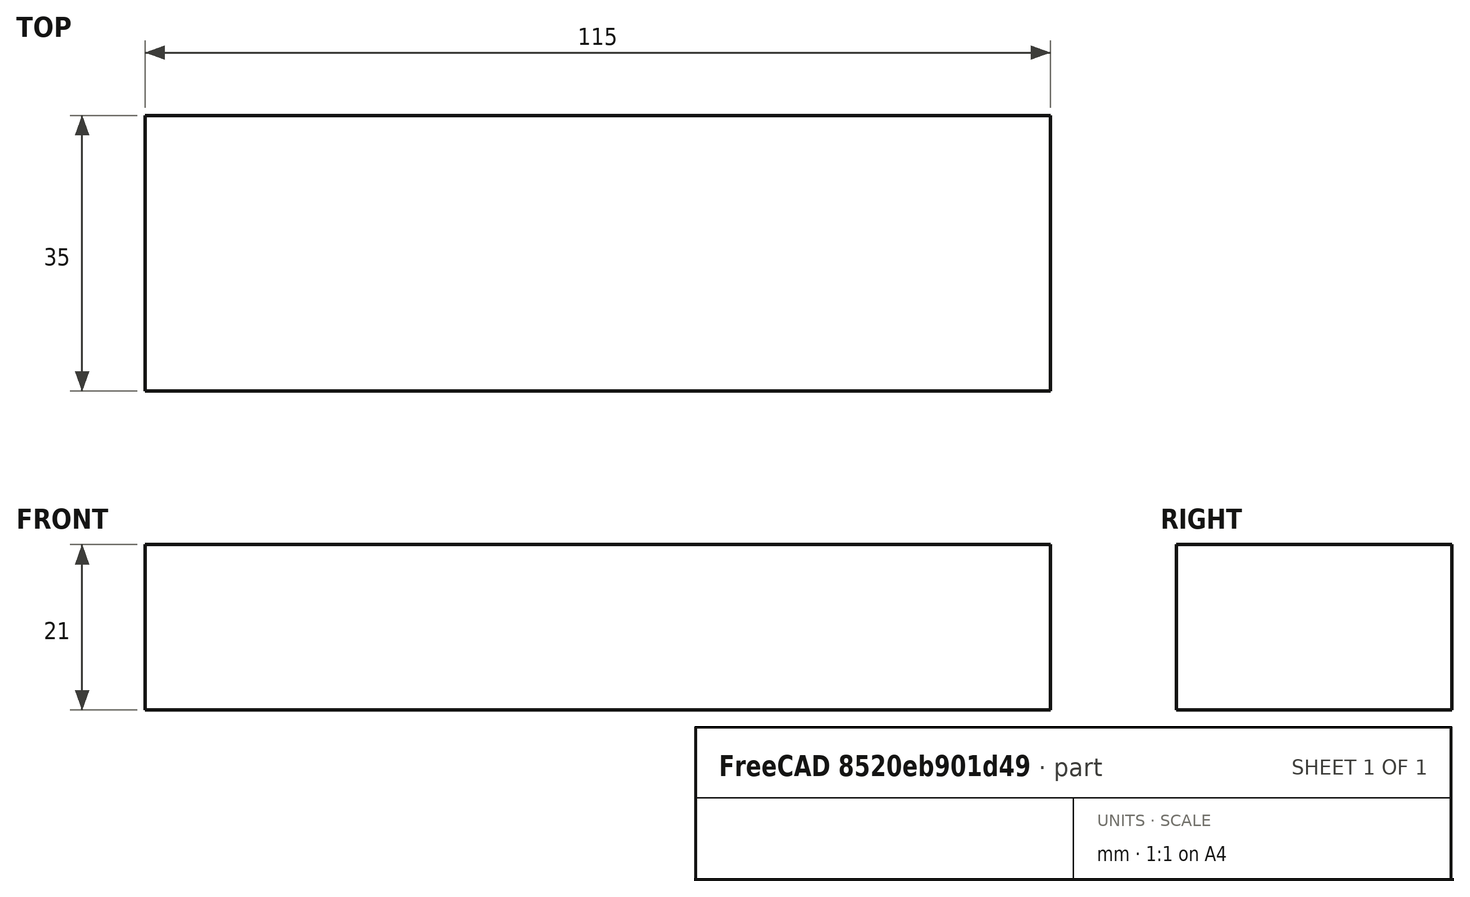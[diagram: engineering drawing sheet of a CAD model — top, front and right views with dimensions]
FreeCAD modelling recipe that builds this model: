
FCSTD DOCUMENT  (FreeCAD 0.18.4R)
Label: baterija1800
License: All rights reserved
LicenseURL: http://en.wikipedia.org/wiki/All_rights_reserved
objects: Sketcher::SketchObject×1, PartDesign::Pad×1, PartDesign::Body×1
note: 4 computed .brp shape members not serialized (recipe doc carries the construction recipe); baked Part::Feature solids carry a one-line shape summary decoded from their .brp

FEATURE [Sketcher::SketchObject] Sketch
  MapMode = 5
  Support = -> [XY_Plane]
  sketch-geometry (4):
    g0: LineSegment StartX=0 StartY=35 StartZ=0 EndX=115 EndY=35 EndZ=0
    g1: LineSegment StartX=115 StartY=35 StartZ=0 EndX=115 EndY=0 EndZ=0
    g2: LineSegment StartX=115 StartY=0 StartZ=0 EndX=0 EndY=0 EndZ=0
    g3: LineSegment StartX=0 StartY=0 StartZ=0 EndX=0 EndY=35 EndZ=0
  constraints (11):
    c: Coincident(g0,g1)
    c: Coincident(g1,g2)
    c: Coincident(g2,g3)
    c: Coincident(g3,g0)
    c: Horizontal(g0)
    c: Horizontal(g2)
    c: Vertical(g1)
    c: Vertical(g3)
    c: Coincident(g2,g-1)
    c: Distance(g3) = 35
    c: Distance(g2) = 115
FEATURE [PartDesign::Pad] Pad
  Length = 21
  Length2 = 100
  Profile = -> Sketch
  Type = 0
FEATURE [PartDesign::Body] Body
  Group = -> [Sketch,Pad]
  Origin = -> Origin
  Tip = -> Pad
